# Revit family: 01502_PFVI
name_source: partatom
category: Air Terminals
revit_build: Autodesk Revit MEP 2012 (Build: 20110309_2315(x64)
units: mm (PartAtom-declared; Revit-internal decimal feet)

## types (6) — shared parameters
Cuello Min-Max = 6" a 16" en Incrementos de 2"
Función = Inyección
Manufacturer = INNES
Material = Alum/Acero/Inoxidable
Model = PFVI
Nota = .
Posición de Instalación = Techo
Tipo de Cuello = Redondo
Type Comments = Plenum de fibra de vidrio
URL = https://www.innes.com.mx
Visible_Texto = No

## per-type parameters (varying)
| type | Conect | Description | Diametro_Requerido | Var1 |
| PFVI-06" | 3" | Difusor perforado para Inyección | 6" | 6 |
| PFVI-08" | 4" | Difusor perforado para Inyección | 8" | 8 |
| PFVI-10" | 5" | Difusor perforado para Inyección | 10" | 10 |
| PFVI-12" | 6" | Difusor perforado para Retorno | 12" | 12 |
| PFVI-14" | 7" | Difusor perforado para Retorno | 14" | 14 |
| PFVI-16" | 8" | Difusor perforado para Retorno | 16" | 16 |

## geometry (parser evidence)
native form markers: Blend x5, Sweep x6
no freeform markers — native parametric forms only
